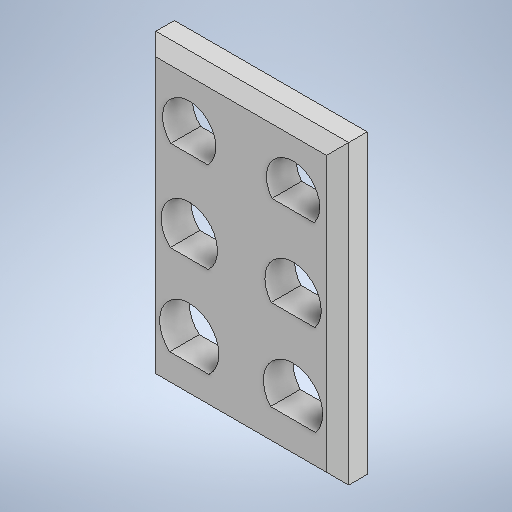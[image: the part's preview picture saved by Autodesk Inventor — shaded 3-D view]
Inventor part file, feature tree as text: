
AUTODESK INVENTOR PART (.ipt)
format: ipt  version: 2025.2 (Build 292293000, 293)  size: 296,448 bytes
history: native  units: in
note: dims shown in document units (in); Inventor stores cm internally (conversion verified against a paired STEP export)
features: sketch x8, extrude x5, hole x3, chamfer x1
ambient origin geometry x8: Origin, YZ Plane, XZ Plane, XY Plane, X Axis, Y Axis, Z Axis, Center Point
bodies: Solid1 (feature_tree)
feature tree (17):
  extrude  "Extrusion1"  Depth=0.7874in
  hole  "Hole3"  [1 undecoded]
  extrude  "Extrusion2"  Depth=0.0787in
  extrude  "Extrusion3"  Depth=0.1575in
  hole  "Hole4"  [1 undecoded]
  extrude  "Extrusion4"  Depth=0.0787in
  hole  "Hole5"  [1 undecoded]
  extrude  "Extrusion5"  Depth=0.0787in TaperAngle=0.0deg
  chamfer  "Chamfer1"  Distance=0.0433in
  sketch  "Sketch1"  dims[d0=0.5118in d1=0.7874in]
  sketch  "Sketch4"  dims[d2=0.3937in d3=0.3937in]
  sketch  "Sketch5"  dims[d4=0.0787in d5=0.0in d20=0.1575in]
  sketch  "Sketch6"  dims[d21=0.1181in d29=0.1575in]
  sketch  "Sketch7"  dims[d30=0.1417in d31=0.2362in d32=0.1575in d33=0.0787in d34=90.0deg d35=0.315in d36=0.8108in d37=0.1181in]
  sketch  "Sketch8"  dims[d38=0.1496in d39=0.2362in d40=0.1575in d41=0.0787in d42=90.0deg d43=0.315in d44=0.8108in d45=0.1181in]
  sketch  "Sketch9"  dims[d46=0.1575in d47=0.1575in]
  sketch  "Sketch10"  dims[d48=0.1575in d49=0.2362in d50=0.1575in d51=0.0787in d52=90.0deg d53=0.315in d54=0.8108in d56=0.0787in d57=0.0in d58=0.0433in d59=0.0787in d60=0.0in d61=0.0551in d62=0.0472in d63=0.0787in d64=0.0in d65=0.0591in d66=0.0512in d67=0.0787in d68=0.0in d69=0.0295in d70=0.0787in d71=45.0deg]
note: 3 required parameter values undecoded (feature->parameter linkage not recoverable at this tier; creation-order binding heuristic only, values carry confidence <= 0.55)
